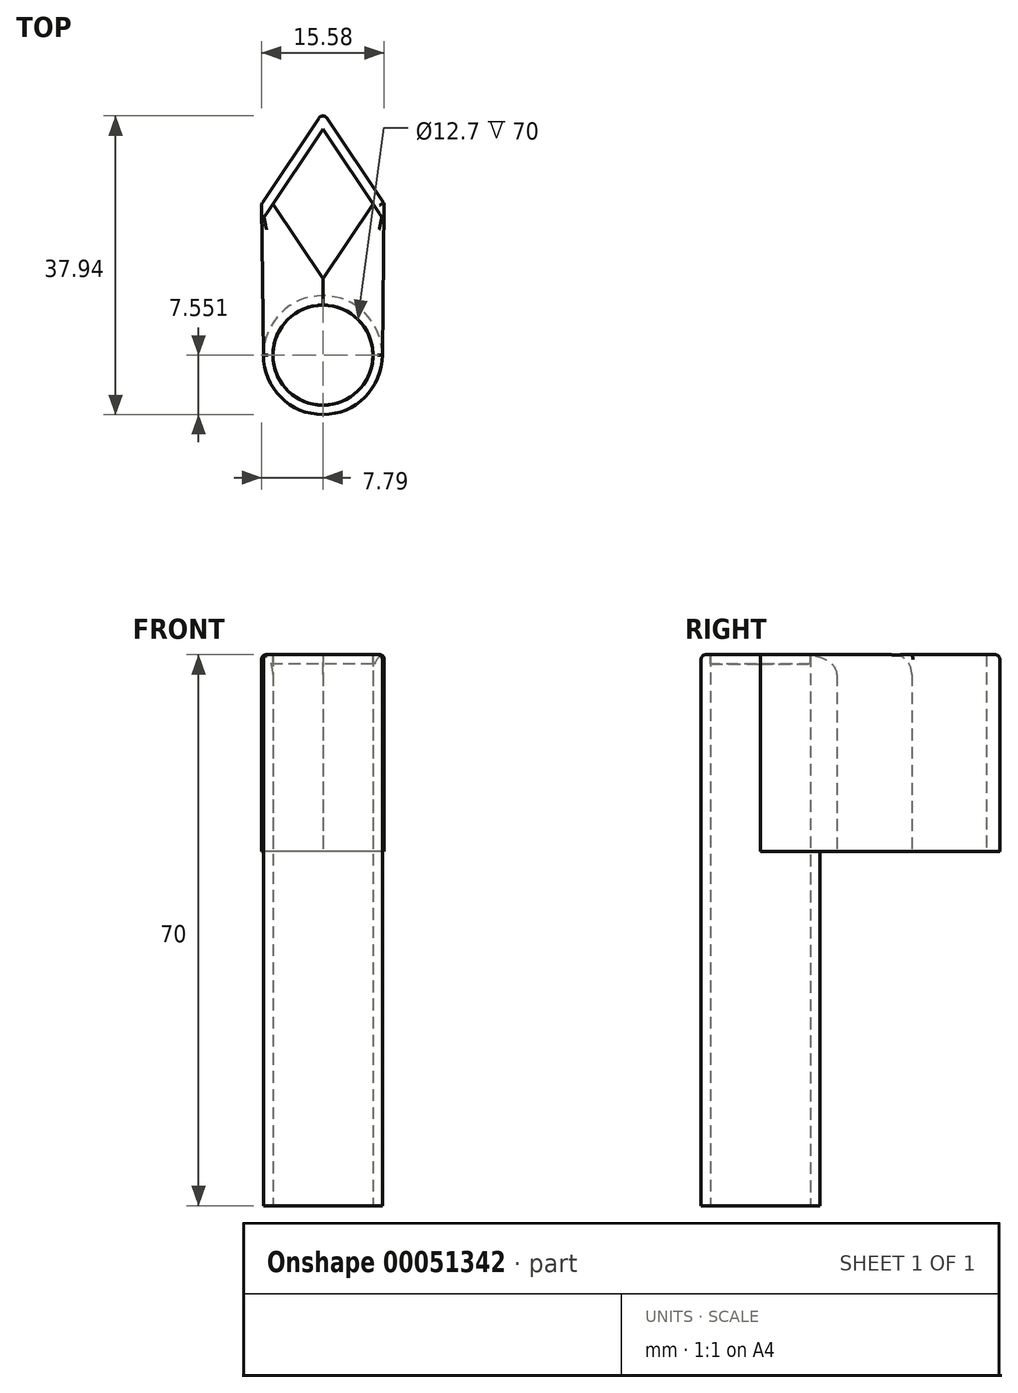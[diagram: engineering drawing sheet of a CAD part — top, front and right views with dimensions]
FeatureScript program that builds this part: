
annotation { "Feature Type Name" : "Feature", "Feature Type Description" : "" }
export const myFeature = defineFeature(function(context is Context, id is Id, definition is map)
    precondition{}
    {
        {
            assignVariable(context, id + "F0", {"name" : "thickness", "anyValue" : 1.2});
        }
        {
            assignVariable(context, id + "F1", {"name" : "starHolderHeight", "anyValue" : 25});
        }
        {
            assignVariable(context, id + "F2", {"name" : "branchHolderHeight", "anyValue" : 70});
        }
        {
            var Q0;
            Q0=qCreatedBy(makeId("Top.planeOp"),FACE);
            var sketch = newSketch(context, id + "F3", { "sketchPlane" : qUnion([Q0])});
            skLineSegment(sketch, "E0", {"start": v(0, 0) * mm, "end": v(0, 9.5) * mm});
            skLineSegment(sketch, "E1", {"start": v(0, 9.5) * mm, "end": v(-6.35, 0) * mm});
            skLineSegment(sketch, "E2", {"start": v(-6.35, 0) * mm, "end": v(0, -9.5) * mm});
            skLineSegment(sketch, "E3", {"start": v(0, -9.5) * mm, "end": v(6.35, 0) * mm});
            skLineSegment(sketch, "E4", {"start": v(6.35, 0) * mm, "end": v(0, 9.5) * mm});
            skLineSegment(sketch, "E5.0", {"start": v(0, 11.66) * mm, "end": v(-7.8, 0) * mm});
            skLineSegment(sketch, "E5.1", {"start": v(7.8, 0) * mm, "end": v(0, 11.66) * mm});
            skLineSegment(sketch, "E5.2", {"start": v(0, -11.66) * mm, "end": v(7.8, 0) * mm});
            skLineSegment(sketch, "E5.3", {"start": v(-7.8, 0) * mm, "end": v(0, -11.66) * mm});
            skSolve(sketch);
        }
        {
            var Q0;
            Q0 = qSketchRegion(id + "F3", true);
            extrude(context, id + "F4", {"entities" : qUnion([Q0]), "depth" : (getVariable(context, 'starHolderHeight')) * mm});
        }
        {
            var Q0;
            Q0=qCreatedBy(makeId("Top.planeOp"),FACE);
            var sketch = newSketch(context, id + "F5", { "sketchPlane" : qUnion([Q0])});
            skCircle(sketch, "E6", {"center": v(0, -19.2) * mm, "radius": 7.55 * mm});
            skCircle(sketch, "E7", {"center": v(0, -19.2) * mm, "radius": 6.35 * mm});
            skLineSegment(sketch, "E8", {"start": v(0, -19.2) * mm, "end": v(-7.55, -19.2) * mm});
            skLineSegment(sketch, "E9", {"start": v(-7.55, -19.2) * mm, "end": v(-7.8, 0) * mm});
            skLineSegment(sketch, "E10", {"start": v(0, -19.2) * mm, "end": v(7.55, -19.2) * mm});
            skLineSegment(sketch, "E11", {"start": v(7.55, -19.2) * mm, "end": v(7.8, 0) * mm});
            skLineSegment(sketch, "E12", {"start": v(-7.8, 0) * mm, "end": v(0, -11.66) * mm});
            skLineSegment(sketch, "E13", {"start": v(0, -11.66) * mm, "end": v(7.8, 0) * mm});
            skSolve(sketch);
        }
        {
            var Q0;
            Q0 = qSketchRegion(id + "F5", true);
            var Q1;
            Q1=makeQuery(id+"F4.opExtrude","CAP_FACE",FACE,{"disambiguationData":[OSD([sQuery(id+"F3.wireOp",EDGE,"E1"),sQuery(id+"F3.wireOp",EDGE,"E2"),sQuery(id+"F3.wireOp",EDGE,"E3"),sQuery(id+"F3.wireOp",EDGE,"E4"),sQuery(id+"F3.wireOp",EDGE,"E5.0"),sQuery(id+"F3.wireOp",EDGE,"E5.1"),sQuery(id+"F3.wireOp",EDGE,"E5.2"),sQuery(id+"F3.wireOp",EDGE,"E5.3")])],"isStart":false});
            extrude(context, id + "F6", {"entities" : qUnion([Q0]), "operationType" : NewBodyOperationType.ADD, "endBound" : BoundingType.UP_TO_SURFACE, "endBoundEntityFace" : qUnion([Q1]), "depth" : 25 * mm});
        }
        {
            var Q0;
            Q0=makeQuery(id+"F6.boolean.opBoolean","MERGE",FACE,{"derivedFrom":[makeQuery(id+"F4.opExtrude","CAP_FACE",FACE,{"disambiguationData":[OSD([sQuery(id+"F3.wireOp",EDGE,"E1"),sQuery(id+"F3.wireOp",EDGE,"E2"),sQuery(id+"F3.wireOp",EDGE,"E3"),sQuery(id+"F3.wireOp",EDGE,"E4"),sQuery(id+"F3.wireOp",EDGE,"E5.0"),sQuery(id+"F3.wireOp",EDGE,"E5.1"),sQuery(id+"F3.wireOp",EDGE,"E5.2"),sQuery(id+"F3.wireOp",EDGE,"E5.3")])],"isStart":true}),makeQuery(id+"F6.opExtrude","CAP_FACE",FACE,{"disambiguationData":[OSD([sQuery(id+"F5.wireOp",EDGE,"E6"),sQuery(id+"F5.wireOp",EDGE,"E7"),sQuery(id+"F5.wireOp",EDGE,"E9"),sQuery(id+"F5.wireOp",EDGE,"E11"),sQuery(id+"F5.wireOp",EDGE,"E12"),sQuery(id+"F5.wireOp",EDGE,"E13")])],"isStart":true})]});
            var sketch = newSketch(context, id + "F7", { "sketchPlane" : qUnion([Q0])});
            skCircle(sketch, "E14", {"center": v(0, 19.2) * mm, "radius": 7.55 * mm});
            skCircle(sketch, "E15.0", {"center": v(0, 19.2) * mm, "radius": 6.35 * mm});
            skSolve(sketch);
        }
        {
            var Q0;
            Q0 = qSketchRegion(id + "F7", true);
            extrude(context, id + "F8", {"entities" : qUnion([Q0]), "operationType" : NewBodyOperationType.ADD, "depth" : (getVariable(context, 'branchHolderHeight') - getVariable(context, 'starHolderHeight')) * mm});
        }
        {
            var Q0;
            Q0=makeQuery(id+"F6.boolean.opBoolean","MERGE",FACE,{"derivedFrom":[makeQuery(id+"F4.opExtrude","CAP_FACE",FACE,{"disambiguationData":[OSD([sQuery(id+"F3.wireOp",EDGE,"E1"),sQuery(id+"F3.wireOp",EDGE,"E2"),sQuery(id+"F3.wireOp",EDGE,"E3"),sQuery(id+"F3.wireOp",EDGE,"E4"),sQuery(id+"F3.wireOp",EDGE,"E5.0"),sQuery(id+"F3.wireOp",EDGE,"E5.1"),sQuery(id+"F3.wireOp",EDGE,"E5.2"),sQuery(id+"F3.wireOp",EDGE,"E5.3")])],"isStart":false}),makeQuery(id+"F6.opExtrude","CAP_FACE",FACE,{"disambiguationData":[OSD([sQuery(id+"F5.wireOp",EDGE,"E6"),sQuery(id+"F5.wireOp",EDGE,"E7"),sQuery(id+"F5.wireOp",EDGE,"E9"),sQuery(id+"F5.wireOp",EDGE,"E11"),sQuery(id+"F5.wireOp",EDGE,"E12"),sQuery(id+"F5.wireOp",EDGE,"E13")])],"isStart":false})]});
            var sketch = newSketch(context, id + "F9", { "sketchPlane" : qUnion([Q0])});
            skCircle(sketch, "E16", {"center": v(0, -19.2) * mm, "radius": 6.35 * mm});
            skSolve(sketch);
        }
        {
            var Q0;
            Q0 = qSketchRegion(id + "F9", true);
            extrude(context, id + "F10", {"entities" : qUnion([Q0]), "oppositeDirection" : true, "depth" : (getVariable(context, 'thickness')) * mm});
        }
        {
            var Q0;
            Q0=makeQuery(id+"F6.opExtrude","CAP_EDGE",EDGE,{"disambiguationData":[OSD([sQuery(id+"F5.wireOp",EDGE,"E11")])],"isStart":false});
            var Q1;
            Q1=makeQuery(id+"F6.opExtrude","CAP_EDGE",EDGE,{"disambiguationData":[OSD([sQuery(id+"F5.wireOp",EDGE,"E6")])],"isStart":false});
            var Q2;
            Q2=makeQuery(id+"F6.opExtrude","CAP_EDGE",EDGE,{"disambiguationData":[OSD([sQuery(id+"F5.wireOp",EDGE,"E9")])],"isStart":false});
            var Q3;
            Q3=makeQuery(id+"F4.opExtrude","CAP_EDGE",EDGE,{"disambiguationData":[OSD([sQuery(id+"F3.wireOp",EDGE,"E5.1")])],"isStart":false});
            var Q4;
            Q4=makeQuery(id+"F4.opExtrude","CAP_EDGE",EDGE,{"disambiguationData":[OSD([sQuery(id+"F3.wireOp",EDGE,"E5.0")])],"isStart":false});
            fillet(context, id + "F11", {"entities" : qUnion([Q0, Q1, Q2, Q3, Q4]), "radius" : 0.6 * mm, "tangentPropagation" : true, "allowEdgeOverflow" : false});
        }
        {
            var Q0;
            Q0=makeQuery(id+"F4.opExtrude","SWEPT_EDGE",EDGE,{"disambiguationData":[OSD([sQuery(id+"F3.wireOp",EDGE,"E5.0"),sQuery(id+"F3.wireOp",EDGE,"E5.1")])]});
            var Q1;
            Q1=makeQuery(id+"F6.boolean.opBoolean","MERGE",EDGE,{"derivedFrom":[makeQuery(id+"F4.opExtrude","SWEPT_EDGE",EDGE,{"disambiguationData":[OSD([sQuery(id+"F3.wireOp",EDGE,"E5.1"),sQuery(id+"F3.wireOp",EDGE,"E5.2")])]}),makeQuery(id+"F6.opExtrude","SWEPT_EDGE",EDGE,{"disambiguationData":[OSD([sQuery(id+"F5.wireOp",EDGE,"E11"),sQuery(id+"F5.wireOp",EDGE,"E13")])]})]});
            var Q2;
            Q2=makeQuery(id+"F6.boolean.opBoolean","MERGE",EDGE,{"derivedFrom":[makeQuery(id+"F4.opExtrude","SWEPT_EDGE",EDGE,{"disambiguationData":[OSD([sQuery(id+"F3.wireOp",EDGE,"E5.0"),sQuery(id+"F3.wireOp",EDGE,"E5.3")])]}),makeQuery(id+"F6.opExtrude","SWEPT_EDGE",EDGE,{"disambiguationData":[OSD([sQuery(id+"F5.wireOp",EDGE,"E9"),sQuery(id+"F5.wireOp",EDGE,"E12")])]})]});
            fillet(context, id + "F12", {"entities" : qUnion([Q0, Q1, Q2]), "radius" : 0.6 * mm, "tangentPropagation" : true, "allowEdgeOverflow" : false});
        }
        {
            var Q0;
            Q0=makeQuery(id+"F4.opExtrude","CAP_EDGE",EDGE,{"disambiguationData":[OSD([sQuery(id+"F3.wireOp",EDGE,"E2")])],"isStart":false});
            var Q1;
            Q1=makeQuery(id+"F4.opExtrude","CAP_EDGE",EDGE,{"disambiguationData":[OSD([sQuery(id+"F3.wireOp",EDGE,"E3")])],"isStart":false});
            fillet(context, id + "F13", {"entities" : qUnion([Q0, Q1]), "radius" : 2.5 * mm, "tangentPropagation" : true, "allowEdgeOverflow" : false});
        }
    });
